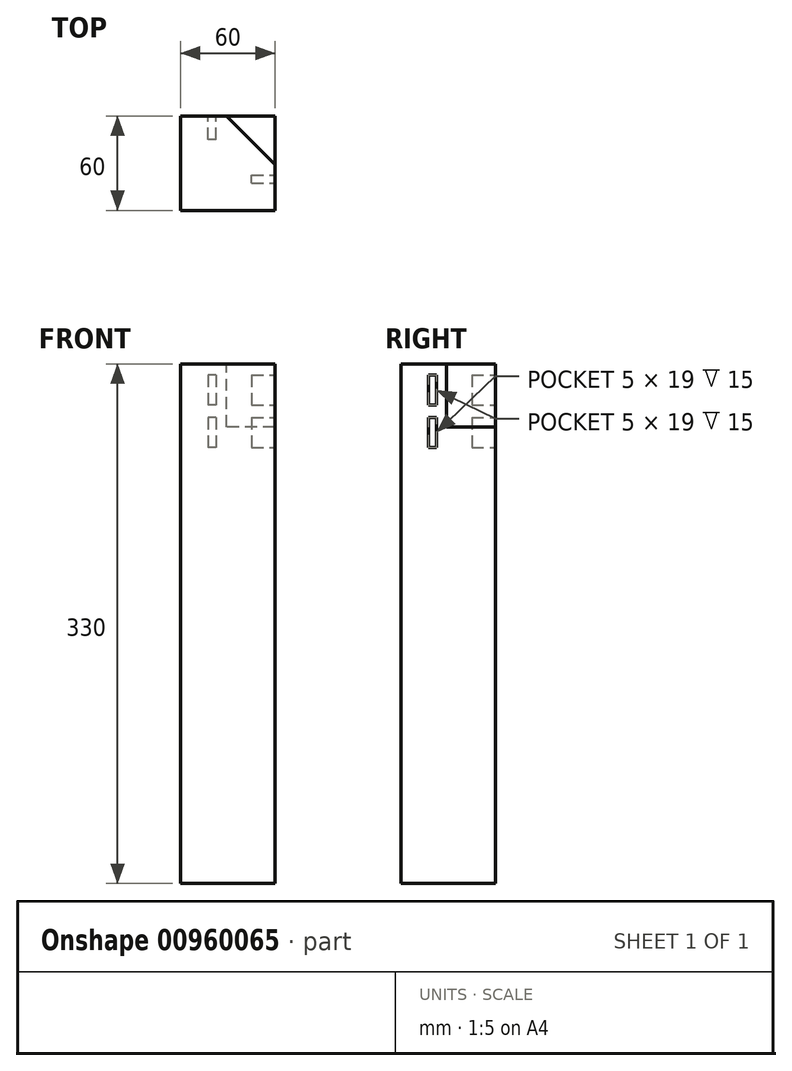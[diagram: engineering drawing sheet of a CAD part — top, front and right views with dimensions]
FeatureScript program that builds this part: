
annotation { "Feature Type Name" : "Feature", "Feature Type Description" : "" }
export const myFeature = defineFeature(function(context is Context, id is Id, definition is map)
    precondition{}
    {
        {
            var Q0;
            Q0=qCreatedBy(makeId("Top.planeOp"),FACE);
            var sketch = newSketch(context, id + "F0", { "sketchPlane" : qUnion([Q0])});
            skLineSegment(sketch, "E0.bottom", {"start": v(30, -30) * mm, "end": v(-30, -30) * mm});
            skLineSegment(sketch, "E0.top", {"start": v(30, 30) * mm, "end": v(-30, 30) * mm});
            skLineSegment(sketch, "E0.left", {"start": v(30, -30) * mm, "end": v(30, 30) * mm});
            skLineSegment(sketch, "E0.right", {"start": v(-30, -30) * mm, "end": v(-30, 30) * mm});
            skPoint(sketch, "E0.middle", {"position": v(0, 0) * mm});
            skSolve(sketch);
        }
        {
            var Q0;
            Q0 = qSketchRegion(id + "F0", true);
            extrude(context, id + "F1", {"entities" : qUnion([Q0]), "oppositeDirection" : true, "depth" : 330 * mm, "offsetDistance" : 25 * mm});
        }
        {
            var Q0;
            Q0=makeQuery(id+"F1.opExtrude","CAP_FACE",FACE,{"disambiguationData":[OSD([sQuery(id+"F0.wireOp",EDGE,"E0.bottom"),sQuery(id+"F0.wireOp",EDGE,"E0.top"),sQuery(id+"F0.wireOp",EDGE,"E0.left"),sQuery(id+"F0.wireOp",EDGE,"E0.right")])],"isStart":true});
            var sketch = newSketch(context, id + "F2", { "sketchPlane" : qUnion([Q0])});
            skLineSegment(sketch, "E1", {"start": v(-1, 30) * mm, "end": v(30, -1) * mm});
            skLineSegment(sketch, "E2", {"start": v(30, -1) * mm, "end": v(30, 30) * mm});
            skLineSegment(sketch, "E3", {"start": v(30, 30) * mm, "end": v(-1, 30) * mm});
            skSolve(sketch);
        }
        {
            var Q0;
            Q0=makeQuery(id+"F2.imprint","IMPRINT",FACE,{"disambiguationData":[TD([[makeQuery(id+"F2.imprint","IMPRINT",EDGE,{"derivedFrom":sQuery(id+"F2.wireOp",EDGE,"E1")}),1.0]])]});
            extrude(context, id + "F3", {"entities" : qUnion([Q0]), "operationType" : NewBodyOperationType.REMOVE, "oppositeDirection" : true, "depth" : 40 * mm, "offsetDistance" : 25 * mm});
        }
        {
            var Q0;
            Q0=makeQuery(id+"F1.opExtrude","SWEPT_FACE",FACE,{"disambiguationData":[OSD([sQuery(id+"F0.wireOp",EDGE,"E0.left")])]});
            var sketch = newSketch(context, id + "F4", { "sketchPlane" : qUnion([Q0])});
            skLineSegment(sketch, "E4.bottom", {"start": v(-12.5, -7) * mm, "end": v(-7.5, -7) * mm});
            skLineSegment(sketch, "E4.top", {"start": v(-12.5, -26) * mm, "end": v(-7.5, -26) * mm});
            skLineSegment(sketch, "E4.left", {"start": v(-12.5, -7) * mm, "end": v(-12.5, -26) * mm});
            skLineSegment(sketch, "E4.right", {"start": v(-7.5, -7) * mm, "end": v(-7.5, -26) * mm});
            skLineSegment(sketch, "E5.bottom", {"start": v(-12.5, -34) * mm, "end": v(-7.5, -34) * mm});
            skLineSegment(sketch, "E5.top", {"start": v(-12.5, -53) * mm, "end": v(-7.5, -53) * mm});
            skLineSegment(sketch, "E5.left", {"start": v(-12.5, -34) * mm, "end": v(-12.5, -53) * mm});
            skLineSegment(sketch, "E5.right", {"start": v(-7.5, -34) * mm, "end": v(-7.5, -53) * mm});
            skSolve(sketch);
        }
        {
            var Q0;
            Q0 = qSketchRegion(id + "F4", true);
            extrude(context, id + "F5", {"entities" : qUnion([Q0]), "operationType" : NewBodyOperationType.REMOVE, "oppositeDirection" : true, "depth" : 15 * mm, "offsetDistance" : 25 * mm});
        }
        {
            var Q0;
            Q0=makeQuery(id+"F1.opExtrude","SWEPT_FACE",FACE,{"disambiguationData":[OSD([sQuery(id+"F0.wireOp",EDGE,"E0.top")])]});
            var sketch = newSketch(context, id + "F6", { "sketchPlane" : qUnion([Q0])});
            skLineSegment(sketch, "E6.bottom", {"start": v(7.5, -7) * mm, "end": v(12.5, -7) * mm});
            skLineSegment(sketch, "E6.top", {"start": v(7.5, -26) * mm, "end": v(12.5, -26) * mm});
            skLineSegment(sketch, "E6.left", {"start": v(7.5, -7) * mm, "end": v(7.5, -26) * mm});
            skLineSegment(sketch, "E6.right", {"start": v(12.5, -7) * mm, "end": v(12.5, -26) * mm});
            skLineSegment(sketch, "E7.bottom", {"start": v(7.5, -34) * mm, "end": v(12.5, -34) * mm});
            skLineSegment(sketch, "E7.top", {"start": v(7.5, -53) * mm, "end": v(12.5, -53) * mm});
            skLineSegment(sketch, "E7.left", {"start": v(7.5, -34) * mm, "end": v(7.5, -53) * mm});
            skLineSegment(sketch, "E7.right", {"start": v(12.5, -34) * mm, "end": v(12.5, -53) * mm});
            skSolve(sketch);
        }
        {
            var Q0;
            Q0=makeQuery(id+"F6.imprint","IMPRINT",FACE,{"disambiguationData":[TD([[makeQuery(id+"F6.imprint","IMPRINT",EDGE,{"derivedFrom":sQuery(id+"F6.wireOp",EDGE,"E6.bottom")}),-1.0]])]});
            var Q1;
            Q1=makeQuery(id+"F6.imprint","IMPRINT",FACE,{"disambiguationData":[TD([[makeQuery(id+"F6.imprint","IMPRINT",EDGE,{"derivedFrom":sQuery(id+"F6.wireOp",EDGE,"E7.bottom")}),-1.0]])]});
            extrude(context, id + "F7", {"entities" : qUnion([Q0, Q1]), "operationType" : NewBodyOperationType.REMOVE, "oppositeDirection" : true, "depth" : 15 * mm, "offsetDistance" : 25 * mm});
        }
    });
